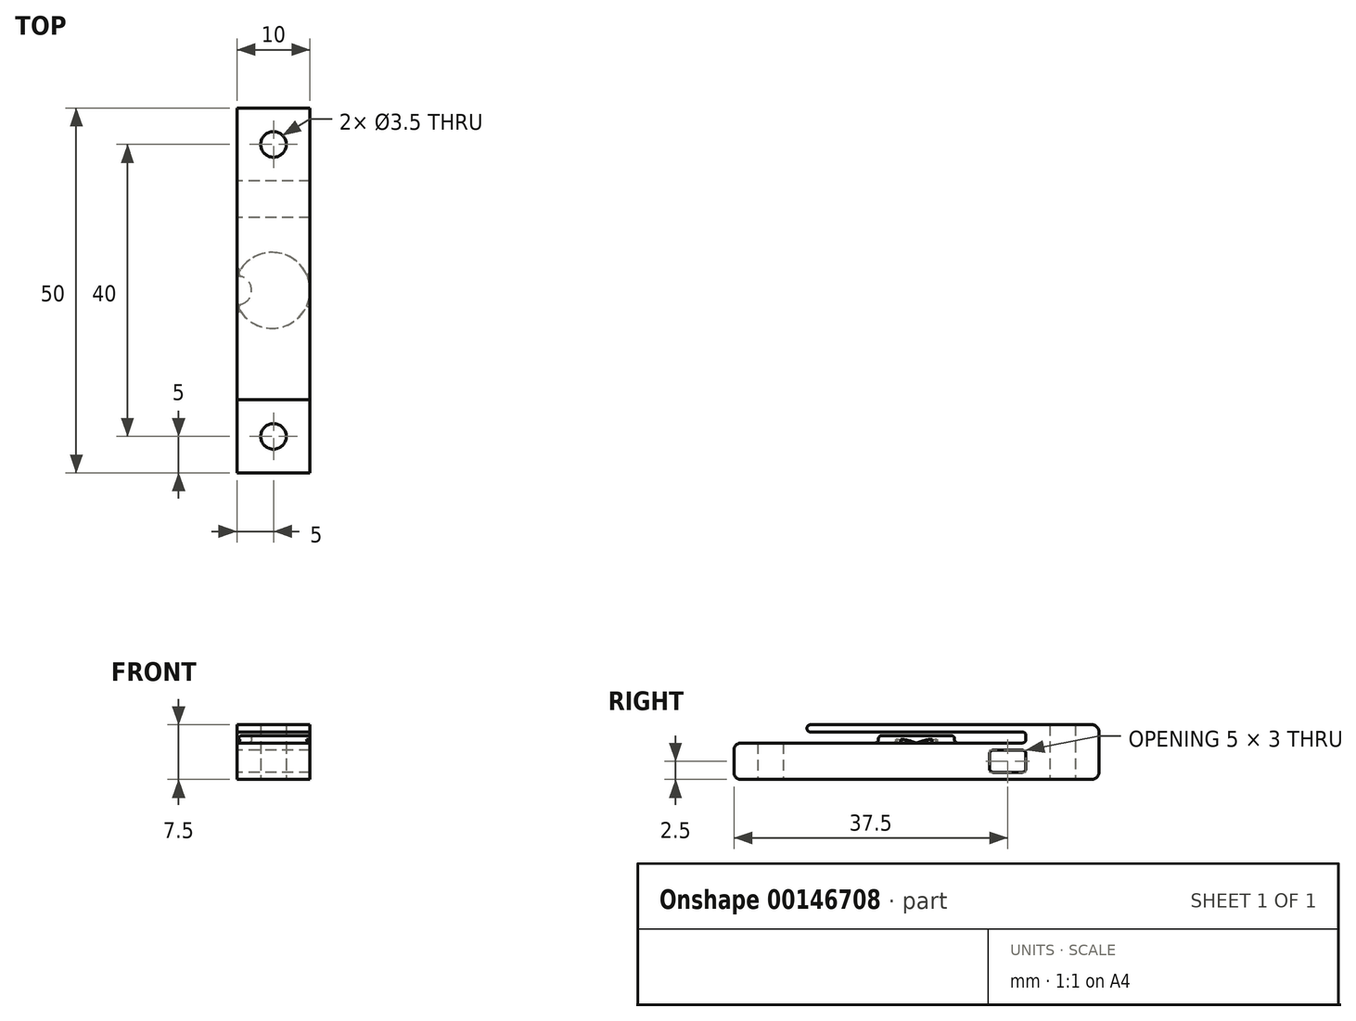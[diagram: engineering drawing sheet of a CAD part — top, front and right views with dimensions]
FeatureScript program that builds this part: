
annotation { "Feature Type Name" : "Feature", "Feature Type Description" : "" }
export const myFeature = defineFeature(function(context is Context, id is Id, definition is map)
    precondition{}
    {
        {
            var Q0;
            Q0=qCreatedBy(makeId("Right.planeOp"),FACE);
            var sketch = newSketch(context, id + "F0", { "sketchPlane" : qUnion([Q0])});
            skLineSegment(sketch, "E0", {"start": v(0, 0) * mm, "end": v(40, 0) * mm});
            skLineSegment(sketch, "E1", {"start": v(40, 0) * mm, "end": v(40, -7.5) * mm});
            skLineSegment(sketch, "E2", {"start": v(40, -7.5) * mm, "end": v(-10, -7.5) * mm});
            skLineSegment(sketch, "E3", {"start": v(-10, -7.5) * mm, "end": v(-10, -2.5) * mm});
            skLineSegment(sketch, "E4", {"start": v(-10, -2.5) * mm, "end": v(30, -2.5) * mm});
            skLineSegment(sketch, "E5", {"start": v(30, -2.5) * mm, "end": v(30, -1) * mm});
            skLineSegment(sketch, "E6", {"start": v(30, -1) * mm, "end": v(0, -1) * mm});
            skLineSegment(sketch, "E7", {"start": v(0, -1) * mm, "end": v(0, 0) * mm});
            skLineSegment(sketch, "E8.bottom", {"start": v(25, -3.5) * mm, "end": v(30, -3.5) * mm});
            skLineSegment(sketch, "E8.top", {"start": v(25, -6.5) * mm, "end": v(30, -6.5) * mm});
            skLineSegment(sketch, "E8.left", {"start": v(25, -3.5) * mm, "end": v(25, -6.5) * mm});
            skLineSegment(sketch, "E8.right", {"start": v(30, -3.5) * mm, "end": v(30, -6.5) * mm});
            skSolve(sketch);
        }
        {
            var Q0;
            Q0=makeQuery(id+"F0.imprint","IMPRINT",FACE,{"disambiguationData":[TD([[makeQuery(id+"F0.imprint","IMPRINT",EDGE,{"derivedFrom":sQuery(id+"F0.wireOp",EDGE,"E0")}),-1.0]])]});
            extrude(context, id + "F1", {"entities" : qUnion([Q0]), "depth" : 10 * mm});
        }
        {
            var Q0;
            Q0=makeQuery(id+"F1.opExtrude","SWEPT_FACE",FACE,{"disambiguationData":[OSD([sQuery(id+"F0.wireOp",EDGE,"E2")])]});
            var sketch = newSketch(context, id + "F2", { "sketchPlane" : qUnion([Q0])});
            skCircle(sketch, "E9", {"center": v(5, -35) * mm, "radius": 1.75 * mm});
            skCircle(sketch, "E10", {"center": v(5, 5) * mm, "radius": 1.75 * mm});
            skLineSegment(sketch, "E11", {"start": v(5, 10) * mm, "end": v(5, -40) * mm, "construction": true});
            skSolve(sketch);
        }
        {
            var Q0;
            Q0 = qSketchRegion(id + "F2", true);
            extrude(context, id + "F3", {"entities" : qUnion([Q0]), "operationType" : NewBodyOperationType.REMOVE, "endBound" : BoundingType.THROUGH_ALL, "oppositeDirection" : true, "depth" : 25 * mm});
        }
        {
            var Q0;
            Q0=makeQuery(id+"F1.opExtrude","SWEPT_FACE",FACE,{"disambiguationData":[OSD([sQuery(id+"F0.wireOp",EDGE,"E4")])]});
            var sketch = newSketch(context, id + "F4", { "sketchPlane" : qUnion([Q0])});
            skArc(sketch, "E12", {"start": v(0, 13) * mm, "mid": v(10, 15) * mm, "end": v(0, 17) * mm});
            skArc(sketch, "E13", {"start": v(0, 13) * mm, "mid": v(2, 15) * mm, "end": v(0, 17) * mm});
            skSolve(sketch);
        }
        {
            var Q0;
            Q0 = qSketchRegion(id + "F4", true);
            extrude(context, id + "F5", {"entities" : qUnion([Q0]), "operationType" : NewBodyOperationType.ADD, "depth" : 1 * mm});
        }
        {
            var Q0;
            Q0=makeQuery(id+"F1.opExtrude","SWEPT_EDGE",EDGE,{"disambiguationData":[OSD([sQuery(id+"F0.wireOp",EDGE,"E5"),sQuery(id+"F0.wireOp",EDGE,"E6")])]});
            var Q1;
            Q1=makeQuery(id+"F1.opExtrude","SWEPT_EDGE",EDGE,{"disambiguationData":[OSD([sQuery(id+"F0.wireOp",EDGE,"E8.bottom"),sQuery(id+"F0.wireOp",EDGE,"E8.right")])]});
            var Q2;
            Q2=makeQuery(id+"F1.opExtrude","SWEPT_EDGE",EDGE,{"disambiguationData":[OSD([sQuery(id+"F0.wireOp",EDGE,"E4"),sQuery(id+"F0.wireOp",EDGE,"E5")])]});
            var Q3;
            Q3=makeQuery(id+"F1.opExtrude","SWEPT_EDGE",EDGE,{"disambiguationData":[OSD([sQuery(id+"F0.wireOp",EDGE,"E8.top"),sQuery(id+"F0.wireOp",EDGE,"E8.right")])]});
            var Q4;
            Q4=makeQuery(id+"F1.opExtrude","SWEPT_EDGE",EDGE,{"disambiguationData":[OSD([sQuery(id+"F0.wireOp",EDGE,"E8.bottom"),sQuery(id+"F0.wireOp",EDGE,"E8.left")])]});
            var Q5;
            Q5=makeQuery(id+"F1.opExtrude","SWEPT_EDGE",EDGE,{"disambiguationData":[OSD([sQuery(id+"F0.wireOp",EDGE,"E8.top"),sQuery(id+"F0.wireOp",EDGE,"E8.left")])]});
            var Q6;
            Q6=makeQuery(id+"F1.opExtrude","SWEPT_EDGE",EDGE,{"disambiguationData":[OSD([sQuery(id+"F0.wireOp",EDGE,"E0"),sQuery(id+"F0.wireOp",EDGE,"E7")])]});
            var Q7;
            Q7=makeQuery(id+"F1.opExtrude","SWEPT_EDGE",EDGE,{"disambiguationData":[OSD([sQuery(id+"F0.wireOp",EDGE,"E6"),sQuery(id+"F0.wireOp",EDGE,"E7")])]});
            fillet(context, id + "F6", {"entities" : qUnion([Q0, Q1, Q2, Q3, Q4, Q5, Q6, Q7]), "radius" : .5 * mm, "tangentPropagation" : true, "allowEdgeOverflow" : false});
        }
        {
            var Q0;
            Q0=makeQuery(id+"F1.opExtrude","SWEPT_EDGE",EDGE,{"disambiguationData":[OSD([sQuery(id+"F0.wireOp",EDGE,"E1"),sQuery(id+"F0.wireOp",EDGE,"E2")])]});
            var Q1;
            Q1=makeQuery(id+"F1.opExtrude","SWEPT_EDGE",EDGE,{"disambiguationData":[OSD([sQuery(id+"F0.wireOp",EDGE,"E0"),sQuery(id+"F0.wireOp",EDGE,"E1")])]});
            var Q2;
            Q2=makeQuery(id+"F1.opExtrude","SWEPT_EDGE",EDGE,{"disambiguationData":[OSD([sQuery(id+"F0.wireOp",EDGE,"E2"),sQuery(id+"F0.wireOp",EDGE,"E3")])]});
            var Q3;
            Q3=makeQuery(id+"F1.opExtrude","SWEPT_EDGE",EDGE,{"disambiguationData":[OSD([sQuery(id+"F0.wireOp",EDGE,"E3"),sQuery(id+"F0.wireOp",EDGE,"E4")])]});
            fillet(context, id + "F7", {"entities" : qUnion([Q0, Q1, Q2, Q3]), "radius" : 1 * mm, "tangentPropagation" : true, "allowEdgeOverflow" : false});
        }
        {
            var Q0;
            {var subQ0=sQuery(id+"F4.wireOp",EDGE,"E13");var subQ1=sQuery(id+"F4.wireOp",EDGE,"E12");var subQ2=sQuery(id+"F0.wireOp",EDGE,"E4");Q0=makeQuery(id+"F5.opExtrude","SWEPT_EDGE",EDGE,{"disambiguationData":[OSD([subQ2,subQ1,subQ0]),TDD([makeQuery(id+"F4.imprint","INTERSECT",VERTEX,{"disambiguationData":[OD(1.0)],"derivedFrom":[makeQuery(id+"F1.opExtrude","CAP_EDGE",EDGE,{"disambiguationData":[OSD([subQ2])],"isStart":true}),subQ1,subQ0]})])]});}
            var Q1;
            {var subQ0=sQuery(id+"F4.wireOp",EDGE,"E13");var subQ1=sQuery(id+"F4.wireOp",EDGE,"E12");var subQ2=sQuery(id+"F0.wireOp",EDGE,"E4");Q1=makeQuery(id+"F5.opExtrude","SWEPT_EDGE",EDGE,{"disambiguationData":[OSD([subQ2,subQ1,subQ0]),TDD([makeQuery(id+"F4.imprint","INTERSECT",VERTEX,{"disambiguationData":[OD(0.0)],"derivedFrom":[makeQuery(id+"F1.opExtrude","CAP_EDGE",EDGE,{"disambiguationData":[OSD([subQ2])],"isStart":true}),subQ1,subQ0]})])]});}
            fillet(context, id + "F8", {"entities" : qUnion([Q0, Q1]), "radius" : .5 * mm, "tangentPropagation" : true, "allowEdgeOverflow" : false});
        }
        {
            var Q0;
            {var subQ0=sQuery(id+"F4.wireOp",EDGE,"E13");var subQ1=sQuery(id+"F4.wireOp",EDGE,"E12");var subQ2=sQuery(id+"F0.wireOp",EDGE,"E4");Q0=makeQuery(id+"F8.opFillet","BLEND_EDGE",EDGE,{"blendedFrom":[makeQuery(id+"F5.opExtrude","SWEPT_EDGE",EDGE,{"disambiguationData":[OSD([subQ2,subQ1,subQ0]),TDD([makeQuery(id+"F4.imprint","INTERSECT",VERTEX,{"disambiguationData":[OD(1.0)],"derivedFrom":[makeQuery(id+"F1.opExtrude","CAP_EDGE",EDGE,{"disambiguationData":[OSD([subQ2])],"isStart":true}),subQ1,subQ0]})])]}),makeQuery(id+"F5.opExtrude","CAP_FACE",FACE,{"disambiguationData":[OSD([subQ1,subQ0])],"isStart":false})],"blendedInto":[makeQuery(id+"F5.opExtrude","CAP_FACE",FACE,{"disambiguationData":[OSD([subQ1,subQ0])],"isStart":false})]});}
            fillet(context, id + "F9", {"entities" : qUnion([Q0]), "radius" : .4 * mm, "tangentPropagation" : true, "allowEdgeOverflow" : false});
        }
        {
            var Q0;
            Q0=makeQuery(id+"F5.boolean.opBoolean","SPLIT",EDGE,{"disambiguationData":[OD(0.0)],"derivedFrom":makeQuery(id+"F5.opExtrude","CAP_EDGE",EDGE,{"disambiguationData":[OSD([sQuery(id+"F4.wireOp",EDGE,"E12")])],"isStart":true})});
            fillet(context, id + "F10", {"entities" : qUnion([Q0]), "radius" : .5 * mm, "tangentPropagation" : true, "allowEdgeOverflow" : false});
        }
    });
